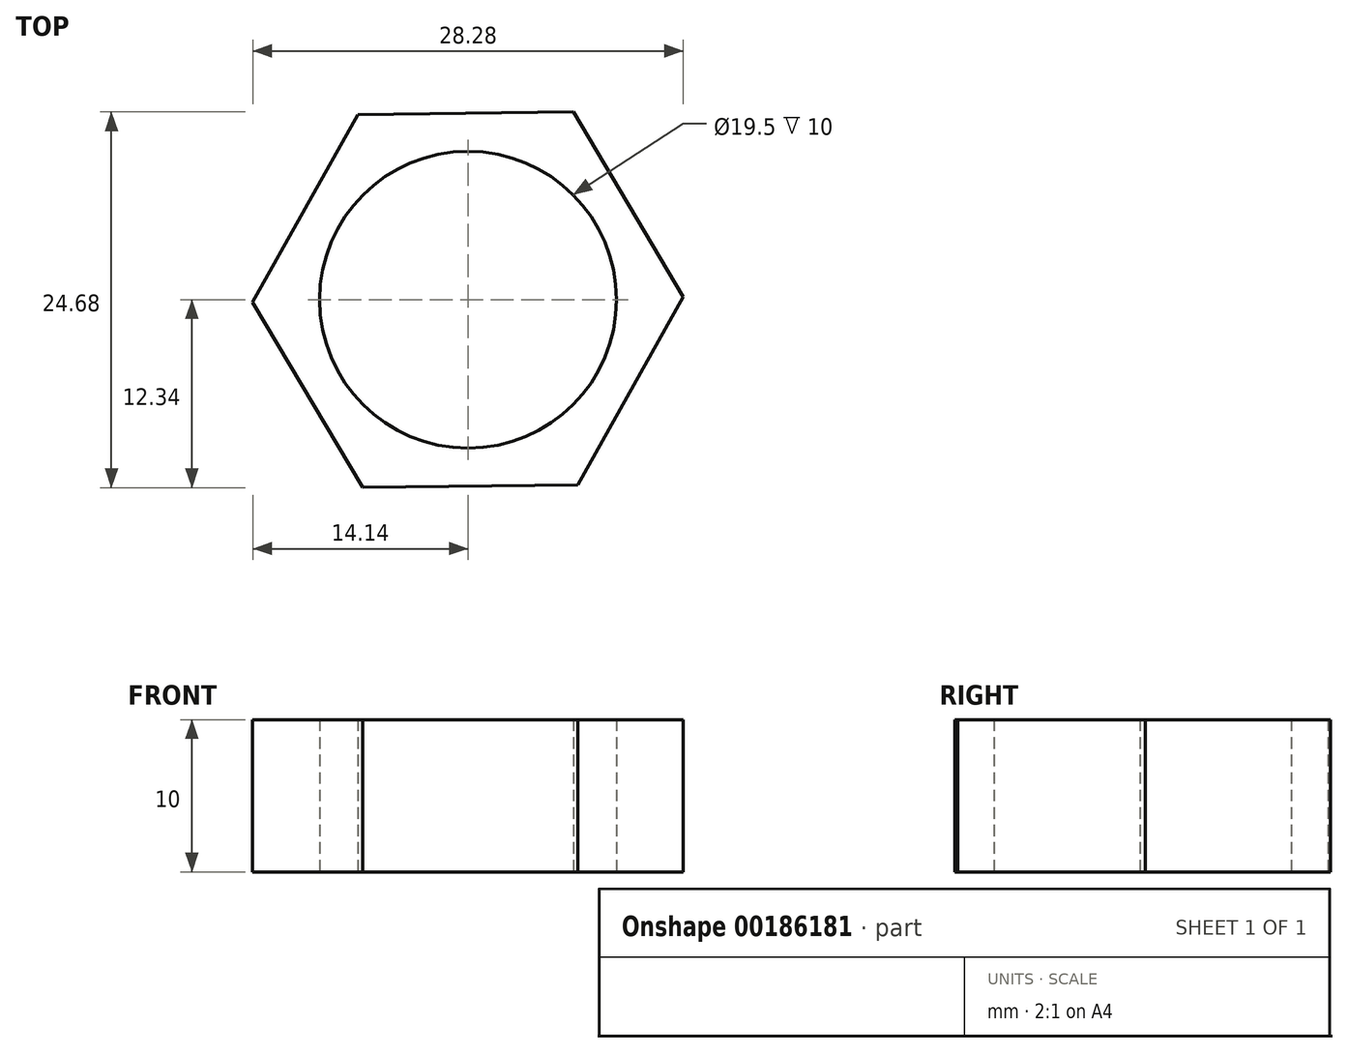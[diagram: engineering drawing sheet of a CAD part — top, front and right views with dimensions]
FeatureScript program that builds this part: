
annotation { "Feature Type Name" : "Feature", "Feature Type Description" : "" }
export const myFeature = defineFeature(function(context is Context, id is Id, definition is map)
    precondition{}
    {
        {
            var Q0;
            Q0=qCreatedBy(makeId("Top.planeOp"),FACE);
            var sketch = newSketch(context, id + "F0", { "sketchPlane" : qUnion([Q0])});
            skCircle(sketch, "E0.cCircle", {"center": v(0, 0) * mm, "radius": 12.25 * mm, "construction": true});
            skLineSegment(sketch, "E0.0", {"start": v(-14.14, -0.18) * mm, "end": v(-7.22, 12.16) * mm});
            skLineSegment(sketch, "E0.1", {"start": v(-7.22, 12.16) * mm, "end": v(6.92, 12.34) * mm});
            skLineSegment(sketch, "E0.2", {"start": v(6.92, 12.34) * mm, "end": v(14.14, 0.18) * mm});
            skLineSegment(sketch, "E0.3", {"start": v(14.14, 0.18) * mm, "end": v(7.22, -12.16) * mm});
            skLineSegment(sketch, "E0.4", {"start": v(7.22, -12.16) * mm, "end": v(-6.92, -12.34) * mm});
            skLineSegment(sketch, "E0.5", {"start": v(-6.92, -12.34) * mm, "end": v(-14.14, -0.18) * mm});
            skPoint(sketch, "E0.0.midPoint", {"position": v(-10.68, 6) * mm});
            skCircle(sketch, "E1", {"center": v(0, 0) * mm, "radius": 9.75 * mm});
            skSolve(sketch);
        }
        {
            var Q0;
            Q0 = qSketchRegion(id + "F0", true);
            extrude(context, id + "F1", {"entities" : qUnion([Q0]), "depth" : 10 * mm});
        }
    });
